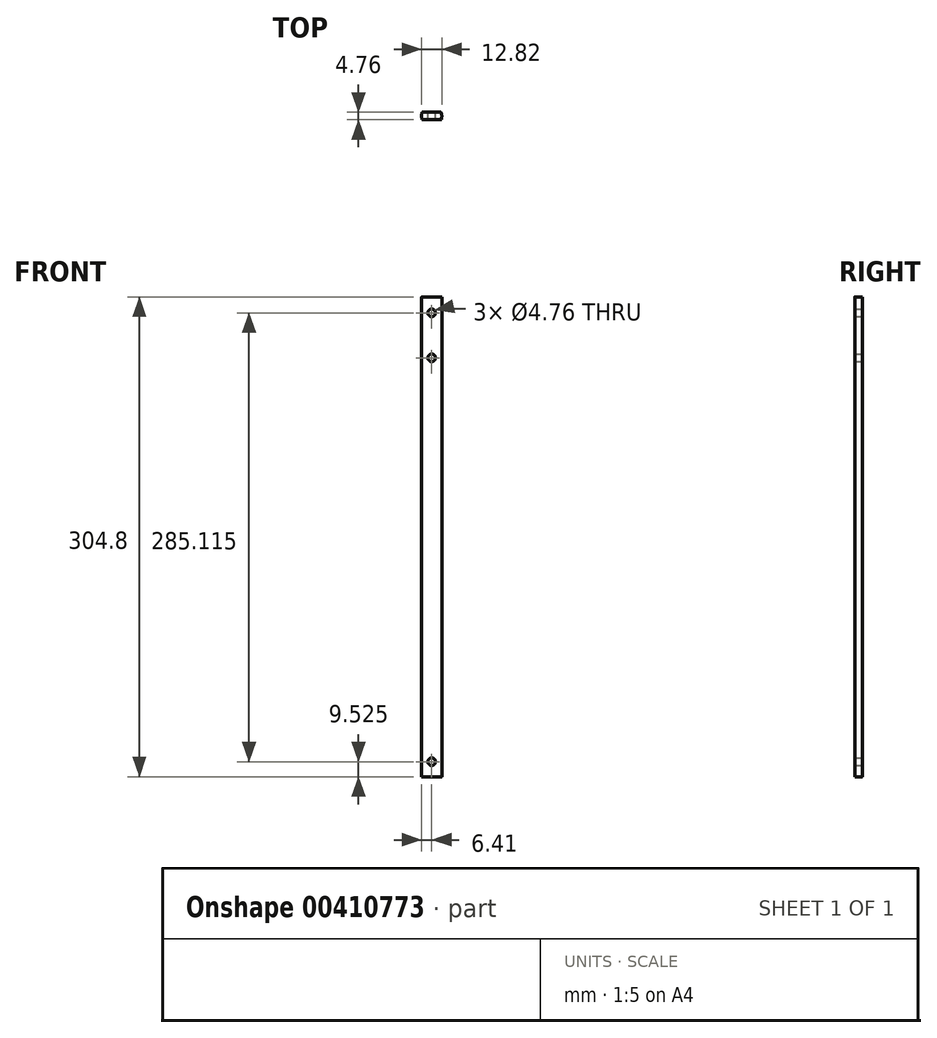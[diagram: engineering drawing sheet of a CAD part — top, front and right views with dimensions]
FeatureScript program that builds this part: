
annotation { "Feature Type Name" : "Feature", "Feature Type Description" : "" }
export const myFeature = defineFeature(function(context is Context, id is Id, definition is map)
    precondition{}
    {
        {
            var Q0;
            Q0=qCreatedBy(makeId("Top.planeOp"),FACE);
            var sketch = newSketch(context, id + "F0", { "sketchPlane" : qUnion([Q0])});
            skLineSegment(sketch, "E0.bottom", {"start": v(5.88, 2.38) * mm, "end": v(-5.9, 2.38) * mm});
            skLineSegment(sketch, "E0.top", {"start": v(5.9, -2.38) * mm, "end": v(-5.88, -2.38) * mm});
            skPoint(sketch, "E0.middle", {"position": v(0, 0) * mm});
            skArc(sketch, "E1", {"start": v(-6.09, 2.24) * mm, "mid": v(-6.41, 0) * mm, "end": v(-6.07, -2.24) * mm});
            skArc(sketch, "E2", {"start": v(6.09, -2.24) * mm, "mid": v(6.41, 0) * mm, "end": v(6.07, 2.24) * mm});
            skPoint(sketch, "E3.visualSharp", {"position": v(-6.04, 2.38) * mm});
            skArc(sketch, "E3.filletArc", {"start": v(-5.9, 2.38) * mm, "mid": v(-6.01, 2.34) * mm, "end": v(-6.09, 2.24) * mm});
            skPoint(sketch, "E4.visualSharp", {"position": v(-6.02, -2.38) * mm});
            skArc(sketch, "E4.filletArc", {"start": v(-6.07, -2.24) * mm, "mid": v(-6, -2.34) * mm, "end": v(-5.88, -2.38) * mm});
            skPoint(sketch, "E5.visualSharp", {"position": v(6.02, 2.38) * mm});
            skArc(sketch, "E5.filletArc", {"start": v(6.07, 2.24) * mm, "mid": v(6, 2.34) * mm, "end": v(5.88, 2.38) * mm});
            skPoint(sketch, "E6.visualSharp", {"position": v(6.04, -2.38) * mm});
            skArc(sketch, "E6.filletArc", {"start": v(5.9, -2.38) * mm, "mid": v(6.01, -2.34) * mm, "end": v(6.09, -2.24) * mm});
            skSolve(sketch);
        }
        {
            var Q0;
            Q0=makeQuery(id+"F0.imprint","IMPRINT",FACE,{"disambiguationData":[TD([[makeQuery(id+"F0.imprint","IMPRINT",EDGE,{"derivedFrom":sQuery(id+"F0.wireOp",EDGE,"E0.bottom")}),1.0]])]});
            extrude(context, id + "F1", {"entities" : qUnion([Q0]), "depth" : 304.8 * mm, "offsetDistance" : 25.4 * mm, "symmetric" : true});
        }
        {
            var Q0;
            Q0=makeQuery(id+"F1.opExtrude","SWEPT_FACE",FACE,{"disambiguationData":[OSD([sQuery(id+"F0.wireOp",EDGE,"E0.bottom")])]});
            var sketch = newSketch(context, id + "F2", { "sketchPlane" : qUnion([Q0])});
            skCircle(sketch, "E7", {"center": v(0, 142.24) * mm, "radius": 2.38 * mm});
            skCircle(sketch, "E8", {"center": v(0, 113.67) * mm, "radius": 2.38 * mm});
            skCircle(sketch, "E9", {"center": v(0, -142.88) * mm, "radius": 2.38 * mm});
            skSolve(sketch);
        }
        {
            var Q0;
            Q0=makeQuery(id+"F2.imprint","IMPRINT",FACE,{"disambiguationData":[TD([[makeQuery(id+"F2.imprint","IMPRINT",EDGE,{"derivedFrom":sQuery(id+"F2.wireOp",EDGE,"E7")}),1.0]])]});
            var Q1;
            Q1=makeQuery(id+"F2.imprint","IMPRINT",FACE,{"disambiguationData":[TD([[makeQuery(id+"F2.imprint","IMPRINT",EDGE,{"derivedFrom":sQuery(id+"F2.wireOp",EDGE,"E8")}),1.0]])]});
            var Q2;
            Q2=makeQuery(id+"F2.imprint","IMPRINT",FACE,{"disambiguationData":[TD([[makeQuery(id+"F2.imprint","IMPRINT",EDGE,{"derivedFrom":sQuery(id+"F2.wireOp",EDGE,"E9")}),1.0]])]});
            extrude(context, id + "F3", {"entities" : qUnion([Q0, Q1, Q2]), "operationType" : NewBodyOperationType.REMOVE, "endBound" : BoundingType.THROUGH_ALL, "oppositeDirection" : true, "depth" : 25.4 * mm, "offsetDistance" : 25.4 * mm});
        }
    });
